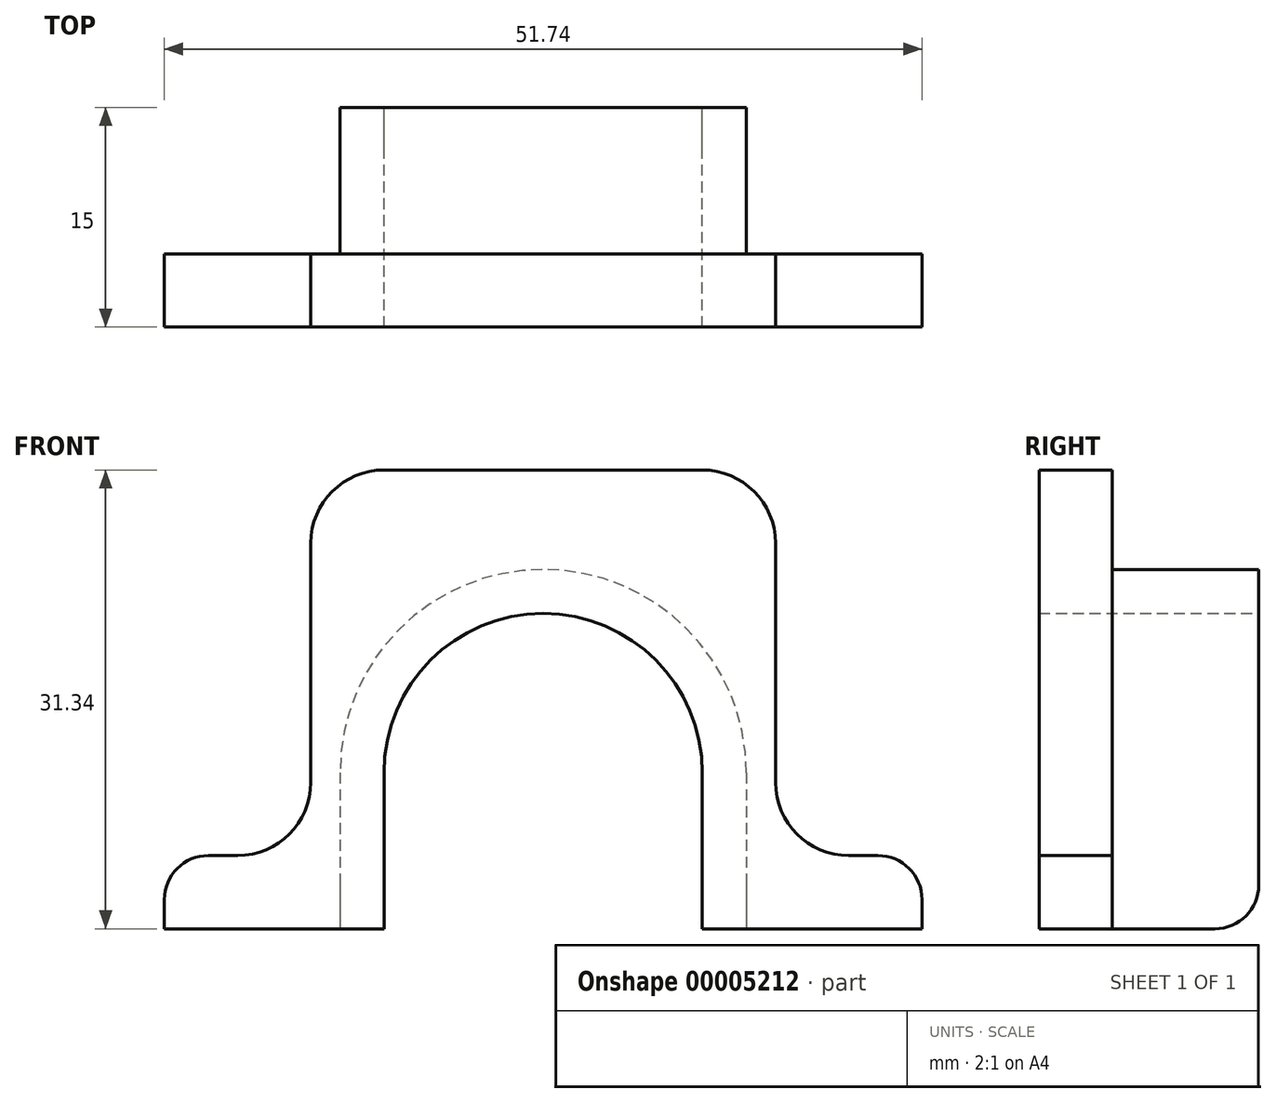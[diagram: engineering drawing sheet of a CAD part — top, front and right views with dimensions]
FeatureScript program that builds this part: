
annotation { "Feature Type Name" : "Feature", "Feature Type Description" : "" }
export const myFeature = defineFeature(function(context is Context, id is Id, definition is map)
    precondition{}
    {
        {
            var Q0;
            Q0=qCreatedBy(makeId("Front.planeOp"),FACE);
            var sketch = newSketch(context, id + "F0", { "sketchPlane" : qUnion([Q0])});
            skCircle(sketch, "E0", {"center": v(0, 0) * mm, "radius": 10.67 * mm, "construction": true});
            skLineSegment(sketch, "E1", {"start": v(0, -10.67) * mm, "end": v(-31.73, -10.67) * mm, "construction": true});
            skArc(sketch, "E2", {"start": v(-10.87, 0) * mm, "mid": v(0, 10.87) * mm, "end": v(10.87, 0) * mm});
            skLineSegment(sketch, "E3", {"start": v(-10.87, 0) * mm, "end": v(-10.87, -10.67) * mm});
            skLineSegment(sketch, "E4", {"start": v(-10.87, -10.67) * mm, "end": v(-25.87, -10.67) * mm});
            skLineSegment(sketch, "E5", {"start": v(-25.87, -10.67) * mm, "end": v(-25.87, -5.67) * mm});
            skLineSegment(sketch, "E6", {"start": v(-25.87, -5.67) * mm, "end": v(-15.87, -5.67) * mm});
            skLineSegment(sketch, "E7", {"start": v(-15.87, -5.67) * mm, "end": v(-15.87, 20.67) * mm});
            skLineSegment(sketch, "E8", {"start": v(0, 0) * mm, "end": v(0, -10.67) * mm, "construction": true});
            skPoint(sketch, "E9", {"position": v(0, 10.67) * mm});
            skPoint(sketch, "E9.positionSnap0", {"position": v(0, 10.87) * mm});
            skLineSegment(sketch, "E10.MirrorCS", {"start": v(10.87, 0) * mm, "end": v(10.87, -10.67) * mm});
            skLineSegment(sketch, "E11.MirrorCS", {"start": v(10.87, -10.67) * mm, "end": v(25.87, -10.67) * mm});
            skLineSegment(sketch, "E12.MirrorCS", {"start": v(25.87, -10.67) * mm, "end": v(25.87, -5.67) * mm});
            skLineSegment(sketch, "E13.MirrorCS", {"start": v(25.87, -5.67) * mm, "end": v(15.87, -5.67) * mm});
            skLineSegment(sketch, "E14.MirrorCS", {"start": v(15.87, -5.67) * mm, "end": v(15.87, 20.67) * mm});
            skLineSegment(sketch, "E15", {"start": v(-15.87, 20.67) * mm, "end": v(15.87, 20.67) * mm});
            skSolve(sketch);
        }
        {
            var Q0;
            Q0 = qSketchRegion(id + "F0", true);
            extrude(context, id + "F1", {"entities" : qUnion([Q0]), "depth" : 5 * mm});
        }
        {
            var Q0;
            Q0=makeQuery(id+"F1.opExtrude","CAP_FACE",FACE,{"disambiguationData":[OSD([sQuery(id+"F0.wireOp",EDGE,"E2"),sQuery(id+"F0.wireOp",EDGE,"E3"),sQuery(id+"F0.wireOp",EDGE,"E4"),sQuery(id+"F0.wireOp",EDGE,"E5"),sQuery(id+"F0.wireOp",EDGE,"E6"),sQuery(id+"F0.wireOp",EDGE,"E7"),sQuery(id+"F0.wireOp",EDGE,"E10.MirrorCS"),sQuery(id+"F0.wireOp",EDGE,"E11.MirrorCS"),sQuery(id+"F0.wireOp",EDGE,"E12.MirrorCS"),sQuery(id+"F0.wireOp",EDGE,"E13.MirrorCS"),sQuery(id+"F0.wireOp",EDGE,"E14.MirrorCS"),sQuery(id+"F0.wireOp",EDGE,"E15")])],"isStart":true});
            var sketch = newSketch(context, id + "F2", { "sketchPlane" : qUnion([Q0])});
            skLineSegment(sketch, "E16.0", {"start": v(-10.87, 0) * mm, "end": v(-10.87, -10.67) * mm});
            skArc(sketch, "E16.1", {"start": v(10.87, 0) * mm, "mid": v(0, 10.87) * mm, "end": v(-10.87, 0) * mm});
            skLineSegment(sketch, "E16.2", {"start": v(10.87, 0) * mm, "end": v(10.87, -10.67) * mm});
            skArc(sketch, "E17", {"start": v(-13.87, 0) * mm, "mid": v(0, 13.87) * mm, "end": v(13.87, 0) * mm});
            skLineSegment(sketch, "E18", {"start": v(-13.87, 0) * mm, "end": v(-13.87, -10.67) * mm});
            skLineSegment(sketch, "E19", {"start": v(-13.87, -10.67) * mm, "end": v(-10.87, -10.67) * mm});
            skLineSegment(sketch, "E20", {"start": v(13.87, 0) * mm, "end": v(13.87, -10.67) * mm});
            skLineSegment(sketch, "E21", {"start": v(13.87, -10.67) * mm, "end": v(10.87, -10.67) * mm});
            skSolve(sketch);
        }
        {
            var Q0;
            Q0 = qSketchRegion(id + "F2", true);
            extrude(context, id + "F3", {"entities" : qUnion([Q0]), "operationType" : NewBodyOperationType.ADD, "depth" : 10 * mm});
        }
        {
            var Q0;
            Q0=makeQuery(id+"F1.opExtrude","SWEPT_EDGE",EDGE,{"disambiguationData":[OSD([sQuery(id+"F0.wireOp",EDGE,"E14.MirrorCS"),sQuery(id+"F0.wireOp",EDGE,"E15")])]});
            var Q1;
            Q1=makeQuery(id+"F1.opExtrude","SWEPT_EDGE",EDGE,{"disambiguationData":[OSD([sQuery(id+"F0.wireOp",EDGE,"E7"),sQuery(id+"F0.wireOp",EDGE,"E15")])]});
            var Q2;
            Q2=makeQuery(id+"F1.opExtrude","SWEPT_EDGE",EDGE,{"disambiguationData":[OSD([sQuery(id+"F0.wireOp",EDGE,"E6"),sQuery(id+"F0.wireOp",EDGE,"E7")])]});
            var Q3;
            Q3=makeQuery(id+"F1.opExtrude","SWEPT_EDGE",EDGE,{"disambiguationData":[OSD([sQuery(id+"F0.wireOp",EDGE,"E13.MirrorCS"),sQuery(id+"F0.wireOp",EDGE,"E14.MirrorCS")])]});
            fillet(context, id + "F4", {"entities" : qUnion([Q0, Q1, Q2, Q3]), "radius" : 5 * mm, "tangentPropagation" : true, "allowEdgeOverflow" : false});
        }
        {
            var Q0;
            Q0=makeQuery(id+"F1.opExtrude","SWEPT_EDGE",EDGE,{"disambiguationData":[OSD([sQuery(id+"F0.wireOp",EDGE,"E5"),sQuery(id+"F0.wireOp",EDGE,"E6")])]});
            var Q1;
            Q1=makeQuery(id+"F1.opExtrude","SWEPT_EDGE",EDGE,{"disambiguationData":[OSD([sQuery(id+"F0.wireOp",EDGE,"E12.MirrorCS"),sQuery(id+"F0.wireOp",EDGE,"E13.MirrorCS")])]});
            var Q2;
            Q2=makeQuery(id+"F3.opExtrude","CAP_EDGE",EDGE,{"disambiguationData":[OSD([sQuery(id+"F2.wireOp",EDGE,"E21")])],"isStart":false});
            var Q3;
            Q3=makeQuery(id+"F3.opExtrude","CAP_EDGE",EDGE,{"disambiguationData":[OSD([sQuery(id+"F2.wireOp",EDGE,"E19")])],"isStart":false});
            var Q4;
            Q4=makeQuery(id+"F3.opExtrude","CAP_EDGE",EDGE,{"disambiguationData":[OSD([sQuery(id+"F2.wireOp",EDGE,"E17")])],"isStart":true});
            fillet(context, id + "F5", {"entities" : qUnion([Q0, Q1, Q2, Q3, Q4]), "radius" : 3 * mm, "tangentPropagation" : true, "allowEdgeOverflow" : false});
        }
    });
